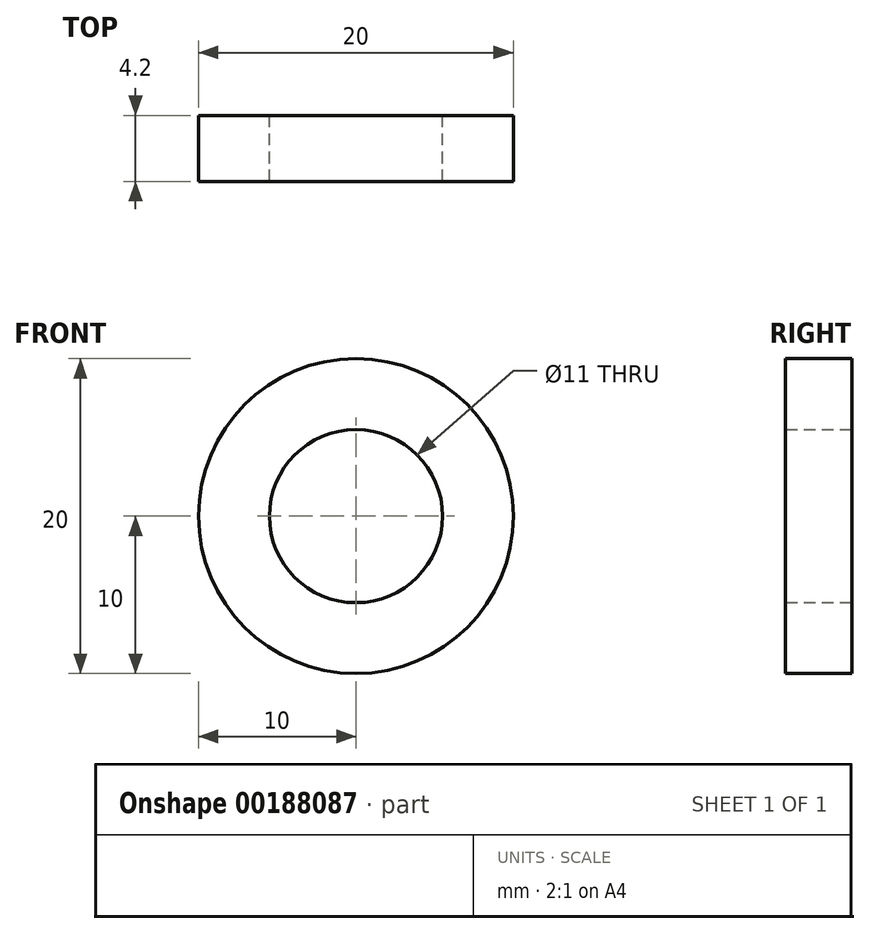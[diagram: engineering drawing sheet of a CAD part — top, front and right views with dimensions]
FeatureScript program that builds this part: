
annotation { "Feature Type Name" : "Feature", "Feature Type Description" : "" }
export const myFeature = defineFeature(function(context is Context, id is Id, definition is map)
    precondition{}
    {
        {
            var Q0;
            Q0=qCreatedBy(makeId("Front.planeOp"),FACE);
            var sketch = newSketch(context, id + "F0", { "sketchPlane" : qUnion([Q0])});
            skCircle(sketch, "E0", {"center": v(0, 0) * mm, "radius": 10 * mm});
            skCircle(sketch, "E1", {"center": v(0, 0) * mm, "radius": 5.5 * mm});
            skSolve(sketch);
        }
        {
            var Q0;
            Q0=makeQuery(id+"F0.imprint","IMPRINT",FACE,{"disambiguationData":[TD([[makeQuery(id+"F0.imprint","IMPRINT",EDGE,{"derivedFrom":sQuery(id+"F0.wireOp",EDGE,"E0")}),1.0]])]});
            extrude(context, id + "F1", {"entities" : qUnion([Q0]), "depth" : 4.2 * mm});
        }
    });
